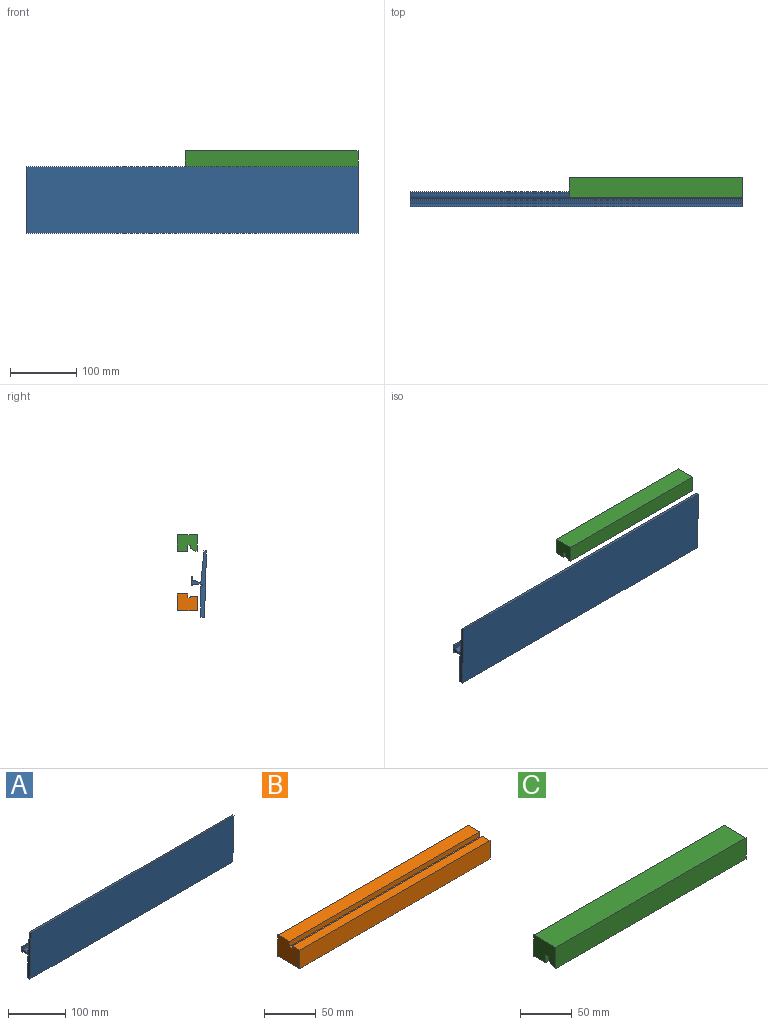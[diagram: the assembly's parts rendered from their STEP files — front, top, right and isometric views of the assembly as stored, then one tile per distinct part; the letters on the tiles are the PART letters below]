
ASSEMBLY  parts=3 mates=3
PART A: 21 faces, bbox 500x22.6x100 mm
  f0: plane 500x48mm, normal (0,1,0.1), area 24109.7mm2, adj f1,f8,f9,f12
  f1: plane 500x3.96mm, normal (0,0,1), area 1978.2mm2, adj f0,f2,f8,f9
  f2: plane 500x99.95mm, normal (0,-1,-0.03), area 50000mm2, adj f1,f3,f8,f9
  f3: plane 500x5.5mm, normal (0,0.03,-1), area 2750mm2, adj f2,f4,f8,f9
  f4: plane 500x44.81mm, normal (0,1,0), area 22402.8mm2, adj f3,f8,f9,f19
  f5: plane 500x0.36mm, normal (0,0.59,0.81), area 220.2mm2, adj f8,f9,f19,f20
  f6: plane 500x1.49mm, normal (0,1,0), area 743.9mm2, adj f7,f8,f9,f20
  f7: plane 500x13mm, normal (0,0,-1), area 6500mm2, adj f6,f8,f9,f15
  f8: plane 99.95x22.55mm, normal (1,0,0), area 654.9mm2, adj f0,f1,f2,f3,f4,f5,f6,f7
  f9: plane 99.95x22.55mm, normal (-1,0,0), area 654.9mm2, adj f0,f1,f2,f3,f4,f5,f6,f7
  f10: plane 500x3.92mm, normal (0,-1,0), area 1960.4mm2, adj f8,f9,f16,f17
  f11: cylinder r=11mm len=500mm, axis (-1,0,0), area 4199mm2, adj f8,f9,f17,f18
  f12: plane 500x2.61mm, normal (0,0,1), area 1303.2mm2, adj f0,f8,f9,f18
  f13: plane 500x11mm, normal (0,1,0), area 5500mm2, adj f8,f9,f14,f16
  f14: cylinder r=1mm len=500mm, axis (1,0,0), area 1570.8mm2, adj f8,f9,f13,f15
  f15: cylinder r=1mm len=500mm, axis (1,0,0), area 785.4mm2, adj f7,f8,f9,f14
  f16: cylinder r=1mm len=500mm, axis (1,0,0), area 1570.8mm2, adj f8,f9,f10,f13
  f17: cylinder r=1mm len=500mm, axis (-1,0,0), area 800.5mm2, adj f8,f9,f10,f11
  f18: cylinder r=1mm len=500mm, axis (-1,0,0), area 366.7mm2, adj f8,f9,f11,f12
  f19: cylinder r=2mm len=500mm, axis (-1,0,0), area 941mm2, adj f4,f5,f8,f9
  f20: cylinder r=2mm len=500mm, axis (1,0,0), area 941mm2, adj f5,f6,f8,f9
PART B: 10 faces, bbox 260x30x25 mm
  f0: plane 260x10.56mm, normal (0,0,1), area 2745.1mm2, adj f1,f7,f8,f9
  f1: plane 260x21.68mm, normal (0,-1,0), area 5636.3mm2, adj f0,f2,f8,f9
  f2: plane 260x30mm, normal (0,0,-1), area 7800mm2, adj f1,f3,f8,f9
  f3: plane 260x25mm, normal (0,1,0), area 6500mm2, adj f2,f4,f8,f9
  f4: plane 260x15.68mm, normal (0,0,1), area 4077.8mm2, adj f3,f5,f8,f9
  f5: plane 260x5.89mm, normal (0,-1,0), area 1530.6mm2, adj f4,f6,f8,f9
  f6: plane 260x3.76mm, normal (0,0,1), area 977.1mm2, adj f5,f7,f8,f9
  f7: plane 260x2.57mm, normal (0,1,0), area 666.9mm2, adj f0,f6,f8,f9
  f8: plane 30x25mm, normal (1,0,0), area 692.8mm2, adj f0,f1,f2,f3,f4,f5,f6,f7
  f9: plane 30x25mm, normal (-1,0,0), area 692.8mm2, adj f0,f1,f2,f3,f4,f5,f6,f7
PART C: 11 faces, bbox 260x30x25 mm
  f0: plane 260x25mm, normal (0,-1,0), area 6500mm2, adj f1,f8,f9,f10
  f1: plane 260x2.48mm, normal (0,0,-1), area 643.7mm2, adj f0,f2,f9,f10
  f2: plane 260x8mm, normal (0,0.47,-0.88), area 2352.3mm2, adj f1,f3,f9,f10
  f3: plane 260x5.11mm, normal (0,1,0.01), area 1327.3mm2, adj f2,f4,f9,f10
  f4: plane 260x3.86mm, normal (0,0,-1), area 1002.3mm2, adj f3,f5,f9,f10
  f5: plane 260x9.33mm, normal (0,-1,0), area 2426.9mm2, adj f4,f6,f9,f10
  f6: plane 260x15.7mm, normal (0,0,-1), area 4082.3mm2, adj f5,f7,f9,f10
  f7: plane 260x25mm, normal (0,1,0), area 6500mm2, adj f6,f8,f9,f10
  f8: plane 260x30mm, normal (0,0,1), area 7800mm2, adj f0,f7,f9,f10
  f9: plane 30x25mm, normal (1,0,0), area 697.3mm2, adj f0,f1,f2,f3,f4,f5,f6,f7
  f10: plane 30x25mm, normal (-1,0,0), area 697.3mm2, adj f0,f1,f2,f3,f4,f5,f6,f7
PLACE A at identity fixed
PLACE B t=(120,4.65,-17.66)mm
PLACE C t=(120,4.65,46.7)mm
MATE planar C.f9 <-> B.f8  axis (1,0,0) through (250,6.49,51.79)mm
MATE planar C.f7 <-> B.f3  axis (0,1,0) through (120,21.18,51.12)mm
MATE planar A.f8 <-> C.f9  axis (1,0,0) through (250,-16.57,-12.45)mm
